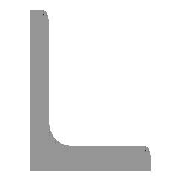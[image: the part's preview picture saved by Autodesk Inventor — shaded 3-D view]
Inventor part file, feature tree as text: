
AUTODESK INVENTOR PART (.ipt)
format: ipt  version: 2017 (Build 210142000, 142)  size: 121,344 bytes
history: native  units: mm (DEFAULTED — no unit token found)
features: other x4, sketch x2, plane x1
ambient origin geometry x8: Origin, YZ Plane, XZ Plane, XY Plane, X Axis, Y Axis, Z Axis, Center Point
bodies: Solid1 (feature_tree), Body (feature_tree)
feature tree (7):
  parser-record x1  (decoder bookkeeping rows leaked as tree rows — omitted from the tree; the rows remain in map.json)
  other  "Driven Length"
  other  "Start plane"
  other  "End plane"
  sketch  "Sketch3"  dims[d0=63.5mm]
  plane  "Work Plane3"
  sketch  "Sketch4"  dims[d1=63.5mm d2=6.35mm d3=6.35mm d4=1155.7mm d5=0.0mm d10=0.0mm d11=0.0mm d12=641.35mm d13=1797.05mm d14=7.874mm d15=3.81mm d16=90.0deg d17=1155.7mm]
